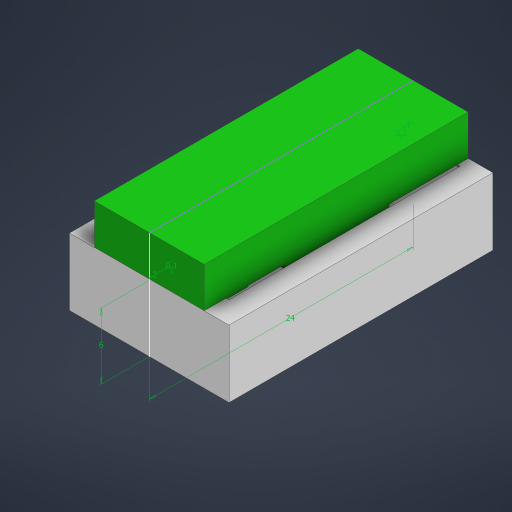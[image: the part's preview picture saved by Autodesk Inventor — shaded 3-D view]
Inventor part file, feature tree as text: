
AUTODESK INVENTOR PART (.ipt)
format: ipt  version: 2024.3 (Build 283343010, 343A)  size: 412,160 bytes
history: native  units: mm
features: extrude x3, sketch x2
ambient origin geometry x8: Origin, YZ Plane, XZ Plane, XY Plane, X Axis, Y Axis, Z Axis, Center Point
bodies: Volumenkörper4 (feature_tree)
feature tree (5):
  sketch  "Skizze3"  dims[d13=24.0mm d14=6.0mm]
  extrude  "Extrusion2"  Depth=6.0mm
  extrude  "Extrusion3"  Depth=0.1mm
  extrude  "Extrusion4"  Depth=1.0mm
  sketch  "Skizze4"  dims[d17=2.0mm d18=0.1mm d19=1.0mm d20=0.1mm d21=10.5mm d22=0.0mm d24=2.0mm d25=24.0mm d26=0.0mm d27=10.0mm d28=2.0mm d29=0.0mm d30=0.0mm d31=2.0mm]
